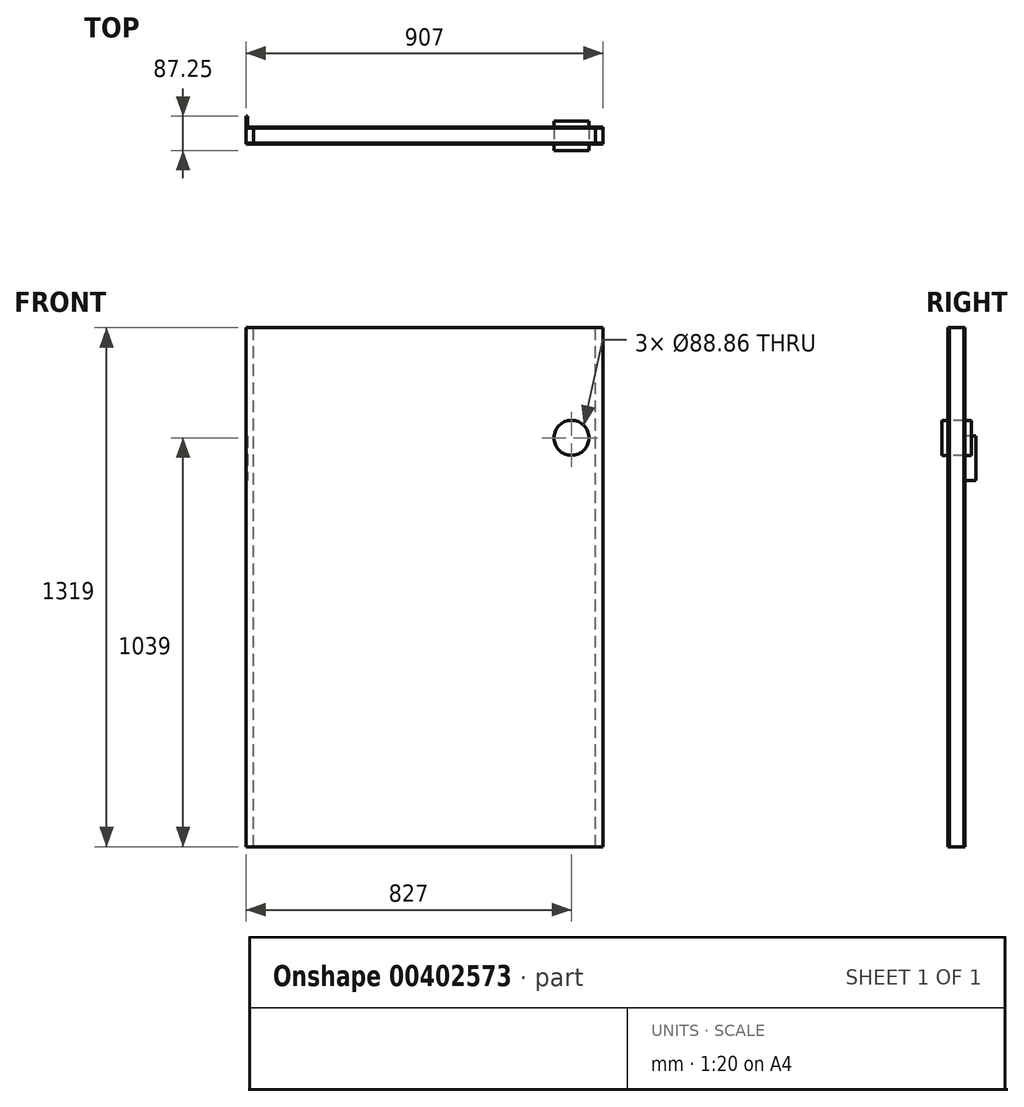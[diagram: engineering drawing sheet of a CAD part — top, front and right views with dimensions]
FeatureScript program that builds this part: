
annotation { "Feature Type Name" : "Feature", "Feature Type Description" : "" }
export const myFeature = defineFeature(function(context is Context, id is Id, definition is map)
    precondition{}
    {
        {
            var Q0;
            Q0=qCreatedBy(makeId("Front.planeOp"),FACE);
            var sketch = newSketch(context, id + "F0", { "sketchPlane" : qUnion([Q0])});
            skLineSegment(sketch, "E0.bottom", {"start": v(-453.5, 659.5) * mm, "end": v(453.5, 659.5) * mm});
            skLineSegment(sketch, "E0.top", {"start": v(-453.5, -659.5) * mm, "end": v(453.5, -659.5) * mm});
            skLineSegment(sketch, "E0.left", {"start": v(-453.5, 659.5) * mm, "end": v(-453.5, -659.5) * mm});
            skLineSegment(sketch, "E0.right", {"start": v(453.5, 659.5) * mm, "end": v(453.5, -659.5) * mm});
            skPoint(sketch, "E0.middle", {"position": v(0, 0) * mm});
            skSolve(sketch);
        }
        {
            var Q0;
            Q0=makeQuery(id+"F0.imprint","IMPRINT",FACE,{"disambiguationData":[TD([[makeQuery(id+"F0.imprint","IMPRINT",EDGE,{"derivedFrom":sQuery(id+"F0.wireOp",EDGE,"E0.bottom")}),-1.0]])]});
            extrude(context, id + "F1", {"entities" : qUnion([Q0]), "depth" : 43.25 * mm});
        }
        {
            var Q0;
            Q0=makeQuery(id+"F1.opExtrude","CAP_FACE",FACE,{"disambiguationData":[OSD([sQuery(id+"F0.wireOp",EDGE,"E0.bottom"),sQuery(id+"F0.wireOp",EDGE,"E0.top"),sQuery(id+"F0.wireOp",EDGE,"E0.left"),sQuery(id+"F0.wireOp",EDGE,"E0.right")])],"isStart":false});
            extrude(context, id + "F2", {"entities" : qUnion([Q0]), "oppositeDirection" : true, "depth" : 2.81 * mm});
        }
        {
            var Q0;
            Q0=makeQuery(id+"F1.opExtrude","CAP_FACE",FACE,{"disambiguationData":[OSD([sQuery(id+"F0.wireOp",EDGE,"E0.bottom"),sQuery(id+"F0.wireOp",EDGE,"E0.top"),sQuery(id+"F0.wireOp",EDGE,"E0.left"),sQuery(id+"F0.wireOp",EDGE,"E0.right")])],"isStart":true});
            extrude(context, id + "F3", {"entities" : qUnion([Q0]), "oppositeDirection" : true, "depth" : 2.81 * mm});
        }
        {
            var Q0;
            Q0=makeQuery(id+"F1.opExtrude","CAP_FACE",FACE,{"disambiguationData":[OSD([sQuery(id+"F0.wireOp",EDGE,"E0.bottom"),sQuery(id+"F0.wireOp",EDGE,"E0.top"),sQuery(id+"F0.wireOp",EDGE,"E0.left"),sQuery(id+"F0.wireOp",EDGE,"E0.right")])],"isStart":false});
            var sketch = newSketch(context, id + "F4", { "sketchPlane" : qUnion([Q0])});
            skLineSegment(sketch, "E1", {"start": v(407.48, 659.5) * mm, "end": v(407.48, 379.5) * mm});
            skLineSegment(sketch, "E2", {"start": v(453.5, 379.5) * mm, "end": v(373.5, 379.5) * mm});
            skPoint(sketch, "E3", {"position": v(373.5, 379.5) * mm});
            skCircle(sketch, "E4", {"center": v(373.5, 379.5) * mm, "radius": 44.43 * mm});
            skSolve(sketch);
        }
        {
            var Q0;
            {var subQ0=sQuery(id+"F4.wireOp",EDGE,"E2");var subQ1=sQuery(id+"F4.wireOp",EDGE,"E1");var subQ2=makeQuery(id+"F4.imprint","INTERSECT",VERTEX,{"derivedFrom":[subQ1,subQ0]});Q0=makeQuery(id+"F4.imprint","IMPRINT",FACE,{"disambiguationData":[TD([[makeQuery(id+"F4.imprint","IMPRINT",EDGE,{"disambiguationData":[TD([[subQ2,1.0]])],"derivedFrom":subQ1}),1.0]])]});}
            var Q1;
            {var subQ0=sQuery(id+"F4.wireOp",EDGE,"E2");var subQ1=sQuery(id+"F4.wireOp",EDGE,"E1");var subQ2=makeQuery(id+"F4.imprint","INTERSECT",VERTEX,{"derivedFrom":[subQ1,subQ0]});Q1=makeQuery(id+"F4.imprint","IMPRINT",FACE,{"disambiguationData":[TD([[makeQuery(id+"F4.imprint","IMPRINT",EDGE,{"disambiguationData":[TD([[subQ2,1.0]])],"derivedFrom":subQ1}),-1.0]])]});}
            extrude(context, id + "F5", {"entities" : qUnion([Q0, Q1]), "operationType" : NewBodyOperationType.REMOVE, "endBound" : BoundingType.THROUGH_ALL, "oppositeDirection" : true, "depth" : 15.73 * mm});
        }
        {
            var Q0;
            Q0=makeQuery(id+"F1.opExtrude","CAP_FACE",FACE,{"disambiguationData":[OSD([sQuery(id+"F0.wireOp",EDGE,"E0.bottom"),sQuery(id+"F0.wireOp",EDGE,"E0.top"),sQuery(id+"F0.wireOp",EDGE,"E0.left"),sQuery(id+"F0.wireOp",EDGE,"E0.right")])],"isStart":true});
            var sketch = newSketch(context, id + "F6", { "sketchPlane" : qUnion([Q0])});
            skPoint(sketch, "E5", {"position": v(450.1, 384.5) * mm});
            skLineSegment(sketch, "E6.bottom", {"start": v(450.1, 384.5) * mm, "end": v(453.5, 384.5) * mm});
            skLineSegment(sketch, "E6.top", {"start": v(450.1, 270.54) * mm, "end": v(453.5, 270.54) * mm});
            skLineSegment(sketch, "E6.left", {"start": v(450.1, 384.5) * mm, "end": v(450.1, 270.54) * mm});
            skLineSegment(sketch, "E6.right", {"start": v(453.5, 384.5) * mm, "end": v(453.5, 270.54) * mm});
            skSolve(sketch);
        }
        {
            var Q0;
            Q0=makeQuery(id+"F6.imprint","IMPRINT",FACE,{"disambiguationData":[TD([[makeQuery(id+"F6.imprint","IMPRINT",EDGE,{"derivedFrom":sQuery(id+"F6.wireOp",EDGE,"E6.bottom")}),-1.0]])]});
            extrude(context, id + "F7", {"entities" : qUnion([Q0]), "depth" : 28 * mm});
        }
        {
            var Q0;
            Q0=makeQuery(id+"F1.opExtrude","CAP_FACE",FACE,{"disambiguationData":[OSD([sQuery(id+"F0.wireOp",EDGE,"E0.bottom"),sQuery(id+"F0.wireOp",EDGE,"E0.top"),sQuery(id+"F0.wireOp",EDGE,"E0.left"),sQuery(id+"F0.wireOp",EDGE,"E0.right")])],"isStart":false});
            var sketch = newSketch(context, id + "F8", { "sketchPlane" : qUnion([Q0])});
            skCircle(sketch, "E7.0", {"center": v(373.5, 379.5) * mm, "radius": 44.43 * mm});
            skSolve(sketch);
        }
        {
            var Q0;
            Q0 = qSketchRegion(id + "F8", true);
            extrude(context, id + "F9", {"entities" : qUnion([Q0]), "depth" : 16 * mm});
        }
        {
            var Q0;
            Q0=makeQuery(id+"F3.opExtrude","CAP_FACE",FACE,{"disambiguationData":[OSD([sQuery(id+"F0.wireOp",EDGE,"E0.bottom"),sQuery(id+"F0.wireOp",EDGE,"E0.top"),sQuery(id+"F0.wireOp",EDGE,"E0.left"),sQuery(id+"F0.wireOp",EDGE,"E0.right")])],"isStart":true});
            var sketch = newSketch(context, id + "F10", { "sketchPlane" : qUnion([Q0])});
            skCircle(sketch, "E8.0", {"center": v(-373.5, 379.5) * mm, "radius": 44.43 * mm});
            skSolve(sketch);
        }
        {
            var Q0;
            Q0 = qSketchRegion(id + "F10", true);
            extrude(context, id + "F11", {"entities" : qUnion([Q0]), "depth" : 16 * mm});
        }
        {
            var Q0;
            Q0=makeQuery(id+"F1.opExtrude","SWEPT_FACE",FACE,{"disambiguationData":[OSD([sQuery(id+"F0.wireOp",EDGE,"E0.bottom")])]});
            var sketch = newSketch(context, id + "F12", { "sketchPlane" : qUnion([Q0])});
            skLineSegment(sketch, "E9", {"start": v(453.5, -40.44) * mm, "end": v(453.5, -2.81) * mm});
            skLineSegment(sketch, "E10", {"start": v(453.5, -2.81) * mm, "end": v(434.5, -2.81) * mm});
            skLineSegment(sketch, "E11", {"start": v(434.5, -2.81) * mm, "end": v(434.5, -2.81) * mm});
            skLineSegment(sketch, "E12", {"start": v(434.5, -40.44) * mm, "end": v(453.5, -40.44) * mm});
            skLineSegment(sketch, "E13", {"start": v(434.5, -2.81) * mm, "end": v(434.5, -40.44) * mm});
            skLineSegment(sketch, "E14.0", {"start": v(-453.5, -40.44) * mm, "end": v(-453.5, -40.44) * mm});
            skLineSegment(sketch, "E15", {"start": v(-453.5, -2.81) * mm, "end": v(-453.5, -2.81) * mm});
            skLineSegment(sketch, "E16", {"start": v(-434.5, -2.81) * mm, "end": v(-434.5, -2.81) * mm});
            skLineSegment(sketch, "E17", {"start": v(-453.5, -2.81) * mm, "end": v(-434.5, -2.81) * mm});
            skLineSegment(sketch, "E18", {"start": v(-453.5, -40.44) * mm, "end": v(-434.5, -40.44) * mm});
            skLineSegment(sketch, "E19", {"start": v(-434.5, -2.81) * mm, "end": v(-434.5, -40.44) * mm});
            skSolve(sketch);
        }
        {
            var Q0;
            {var subQ0=sQuery(id+"F12.wireOp",EDGE,"E17");Q0=makeQuery(id+"F12.imprint","IMPRINT",FACE,{"disambiguationData":[TD([[makeQuery(id+"F12.imprint","IMPRINT",EDGE,{"derivedFrom":subQ0}),-1.0]])]});}
            var Q1;
            Q1=makeQuery(id+"F12.imprint","IMPRINT",FACE,{"disambiguationData":[TD([[makeQuery(id+"F12.imprint","IMPRINT",EDGE,{"derivedFrom":sQuery(id+"F12.wireOp",EDGE,"E9")}),1.0]])]});
            extrude(context, id + "F13", {"entities" : qUnion([Q0, Q1]), "endBound" : BoundingType.UP_TO_NEXT, "oppositeDirection" : true, "depth" : 25 * mm});
        }
    });
